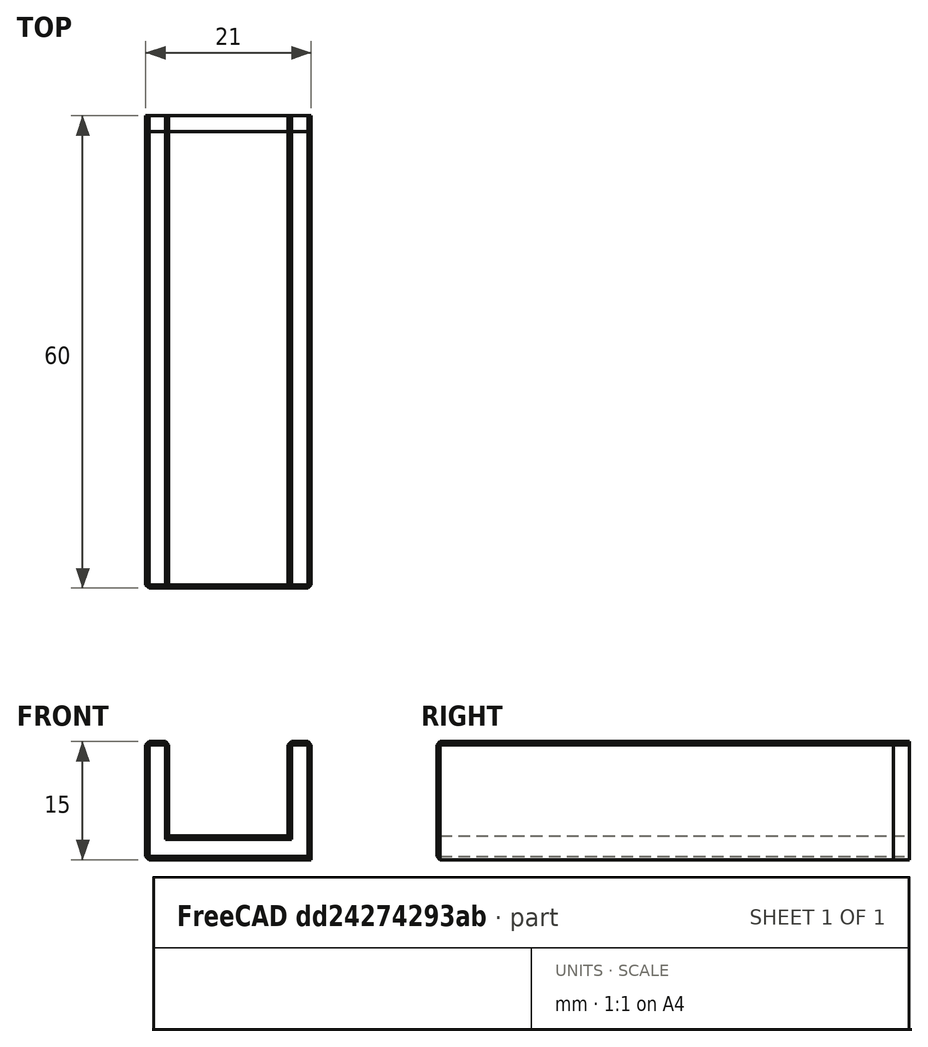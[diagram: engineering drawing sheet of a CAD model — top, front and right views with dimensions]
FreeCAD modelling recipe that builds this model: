
FCSTD DOCUMENT  (FreeCAD 0.18R16146 (Git))
Label: aligner
License: All rights reserved
LicenseURL: http://en.wikipedia.org/wiki/All_rights_reserved
objects: Part::Box×3, Part::Cut×1, Part::Chamfer×1, Part::Feature×1, Part::MultiCommon×1
note: 7 computed .brp shape members not serialized (recipe doc carries the construction recipe); baked Part::Feature solids carry a one-line shape summary decoded from their .brp

FEATURE [Part::Box] Box  label="Cube"
  AttacherType = Attacher::AttachEngine3D
  Height = 15
  Length = 15.2
  Placement = pos=(-7.6,0,3) rot=(0,0,1;0rad)
  Width = 60
FEATURE [Part::Box] Box001  label="Cube001"
  AttacherType = Attacher::AttachEngine3D
  Height = 15
  Length = 21
  Placement = pos=(-10.5,0,0) rot=(0,0,1;0rad)
  Width = 60
FEATURE [Part::Cut] Cut
  Base = -> Box001
  Tool = -> Box
FEATURE [Part::Chamfer] Chamfer  label="pref"
  Base = -> Cut
  Edges = 13 edges r=0.4: [Edge1,Edge2,Edge4,Edge5,Edge6,Edge7,Edge8,Edge9,Edge10,Edge11,Edge13,Edge21,Edge22]
FEATURE [Part::Box] Box002  label="Cube002"
  AttacherType = Attacher::AttachEngine3D
  Height = 17
  Length = 22
  Placement = pos=(-11,0,0) rot=(0,0,1;0rad)
  Width = 58
FEATURE [Part::Feature] Chamfer001  label="pref001"
  shape: bbox 21 x 60 x 15 mm, 28 faces (baked)
FEATURE [Part::MultiCommon] Common
  Shapes = -> [Box002,Chamfer001]
